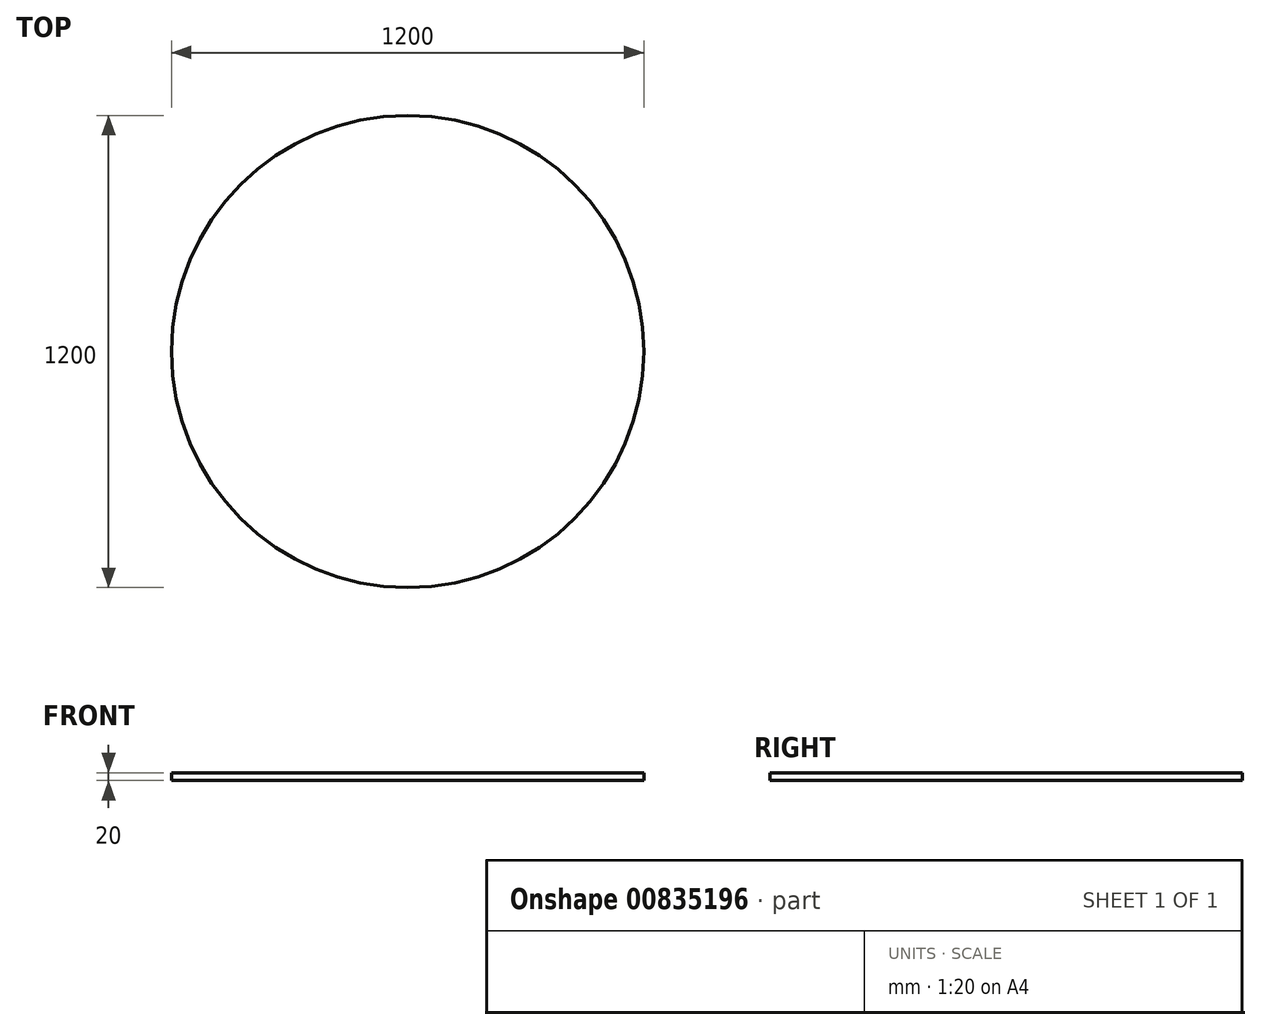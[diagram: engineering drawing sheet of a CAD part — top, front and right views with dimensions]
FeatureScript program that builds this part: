
annotation { "Feature Type Name" : "Feature", "Feature Type Description" : "" }
export const myFeature = defineFeature(function(context is Context, id is Id, definition is map)
    precondition{}
    {
        {
            var Q0;
            Q0=qCreatedBy(makeId("Top.planeOp"),FACE);
            var sketch = newSketch(context, id + "F0", { "sketchPlane" : qUnion([Q0])});
            skCircle(sketch, "E0", {"center": v(0, 0) * mm, "radius": 600 * mm});
            skSolve(sketch);
        }
        {
            var Q0;
            Q0=makeQuery(id+"F0.imprint","IMPRINT",FACE,{"disambiguationData":[TD([[makeQuery(id+"F0.imprint","IMPRINT",EDGE,{"derivedFrom":sQuery(id+"F0.wireOp",EDGE,"E0")}),1.0]])]});
            extrude(context, id + "F1", {"entities" : qUnion([Q0]), "depth" : 20 * mm, "offsetDistance" : 25 * mm});
        }
    });
